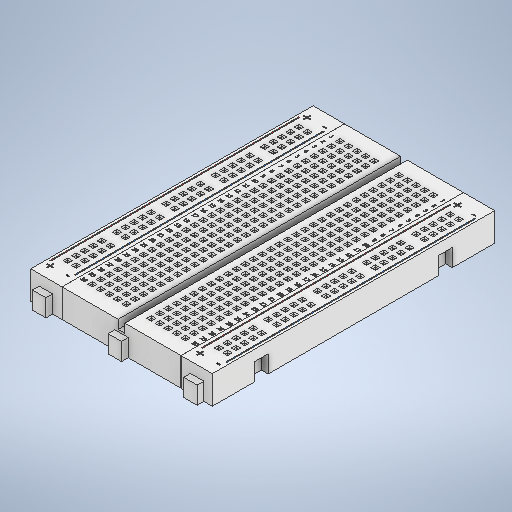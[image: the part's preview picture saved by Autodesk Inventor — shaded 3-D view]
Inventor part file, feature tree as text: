
AUTODESK INVENTOR PART (.ipt)
format: ipt  version: 2025.1 (Build 291241020, 241B)  size: 5,369,856 bytes
history: native  units: mm
features: sketch x15, extrude x14, other x4, chamfer x2, pattern_linear x2, mirror x1
ambient origin geometry x8: Origin, YZ Plane, XZ Plane, XY Plane, X Axis, Y Axis, Z Axis, Center Point
bodies: Solido1 (feature_tree)
feature tree (38):
  extrude  "Estrusione1"  Depth=84.0mm
  extrude  "Estrusione2"  Depth=5.2mm
  extrude  "Estrusione3"  Depth=4.0mm
  extrude  "Estrusione4"  Depth=12.6mm
  extrude  "Estrusione5"  Depth=12.6mm
  extrude  "Estrusione6"  Depth=58.8mm
  extrude  "Estrusione7"  Depth=2.0mm TaperAngle=0.0deg
  sketch  "Schizzo11"
  extrude  "Estrusione8"  Depth=2.0mm TaperAngle=0.0deg
  extrude  "Estrusione9"  Depth=4.0mm
  sketch  "Schizzo12"
  extrude  "Estrusione10"  Depth=4.0mm
  extrude  "Estrusione11"  Depth=4.0mm
  extrude  "Estrusione12"  Depth=2.5mm
  chamfer  "Smusso1"  Distance=2.5mm
  pattern_linear  "Serie rettangolare1"  Spacing1=2.0mm  [1 undecoded]
  extrude  "Estrusione13"  Depth=2.0mm TaperAngle=0.0deg
  chamfer  "Smusso2"  Distance=2.0mm
  pattern_linear  "Serie rettangolare2"  Spacing1=2.6mm  [1 undecoded]
  other  "Piano di lavoro1"
  mirror  "Specchio1"
  extrude  "Estrusione14"  TaperAngle=0.0deg  [1 undecoded]
  sketch  "Schizzo4"
  sketch  "Schizzo5"
  sketch  "Schizzo6"
  sketch  "Schizzo7"
  sketch  "Schizzo8"
  other  "Linea chiusa proiettata1"
  other  "Linea chiusa proiettata2"
  other  "Linea chiusa proiettata3"
  sketch  "Schizzo9"
  sketch  "Schizzo10"
  sketch  "Schizzo13"
  sketch  "Sketch Rectangular Pattern1"  dims[d0=54.0mm d1=84.0mm]
  sketch  "Sketch Rectangular Pattern2"  dims[d2=8.4mm d3=0.0mm d4=5.2mm]
  sketch  "Schizzo14"
  sketch  "Sketch Rectangular Pattern3"  dims[d5=4.0mm d6=4.0mm d7=12.6mm d9=12.6mm d10=58.8mm d11=2.0mm d12=0.0mm d13=2.0mm d14=0.0mm d15=4.0mm d16=4.0mm d17=4.0mm d18=2.5mm d19=2.5mm d20=2.0mm d21=0.0mm d22=2.0mm d23=0.0mm d24=2.0mm d25=2.6mm d26=0.0mm d27=0.0mm d28=9.3mm d29=9.3mm d30=0.01mm d31=0.01mm d32=10.0mm d33=0.0mm d34=0.3mm d35=74.0mm d36=0.7mm d37=0.01mm d38=0.0mm d39=0.01mm d40=0.0mm d41=0.01mm d42=0.0mm d43=0.01mm d44=0.0mm d45=0.8mm d46=0.8mm d47=20.0mm d49=2.54mm d50=50.0mm d52=2.54mm d55=7.2mm d56=2.98mm d57=2.98mm d58=50.0mm d60=14.66mm d61=10.0mm d63=10.0mm d65=7.2mm d66=2.5mm d67=0.0mm d68=0.3mm d69=2.0mm d70=45.0deg d71=20.0mm d73=45.0mm d74=50.0mm d76=2.54mm d77=300.0mm d79=2.54mm d82=4.77mm d83=4.77mm d84=2.3mm d85=2.5mm d86=0.0mm d87=0.3mm d88=2.0mm d89=45.0deg d90=50.0mm d92=2.54mm d93=300.0mm d95=2.54mm d96=0.01mm d97=0.0mm]
  sketch  "Schizzo15"
note: 3 required parameter values undecoded (feature->parameter linkage not recoverable at this tier; creation-order binding heuristic only, values carry confidence <= 0.55)
